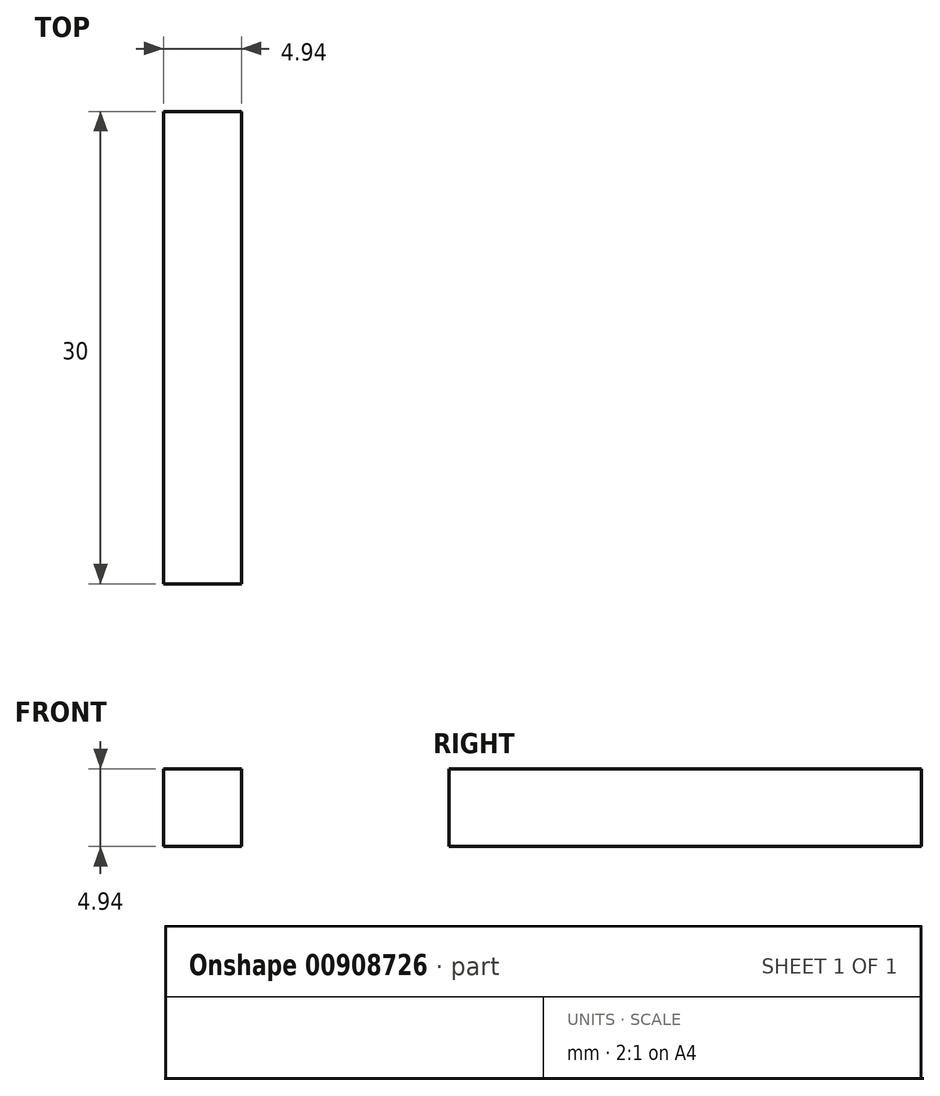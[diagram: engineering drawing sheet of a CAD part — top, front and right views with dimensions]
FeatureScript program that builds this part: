
annotation { "Feature Type Name" : "Feature", "Feature Type Description" : "" }
export const myFeature = defineFeature(function(context is Context, id is Id, definition is map)
    precondition{}
    {
        {
            var Q0;
            Q0=qCreatedBy(makeId("Front.planeOp"),FACE);
            var sketch = newSketch(context, id + "F0", { "sketchPlane" : qUnion([Q0])});
            skLineSegment(sketch, "E0.bottom", {"start": v(2.47, 2.47) * mm, "end": v(-2.47, 2.47) * mm});
            skLineSegment(sketch, "E0.top", {"start": v(2.47, -2.47) * mm, "end": v(-2.47, -2.47) * mm});
            skLineSegment(sketch, "E0.left", {"start": v(2.47, 2.47) * mm, "end": v(2.47, -2.47) * mm});
            skLineSegment(sketch, "E0.right", {"start": v(-2.47, 2.47) * mm, "end": v(-2.47, -2.47) * mm});
            skPoint(sketch, "E0.middle", {"position": v(0, 0) * mm});
            skSolve(sketch);
        }
        {
            var Q0;
            Q0=makeQuery(id+"F0.imprint","IMPRINT",FACE,{"disambiguationData":[TD([[makeQuery(id+"F0.imprint","IMPRINT",EDGE,{"derivedFrom":sQuery(id+"F0.wireOp",EDGE,"E0.bottom")}),1.0]])]});
            extrude(context, id + "F1", {"entities" : qUnion([Q0]), "depth" : 30 * mm, "offsetDistance" : 25 * mm, "symmetric" : true});
        }
    });
